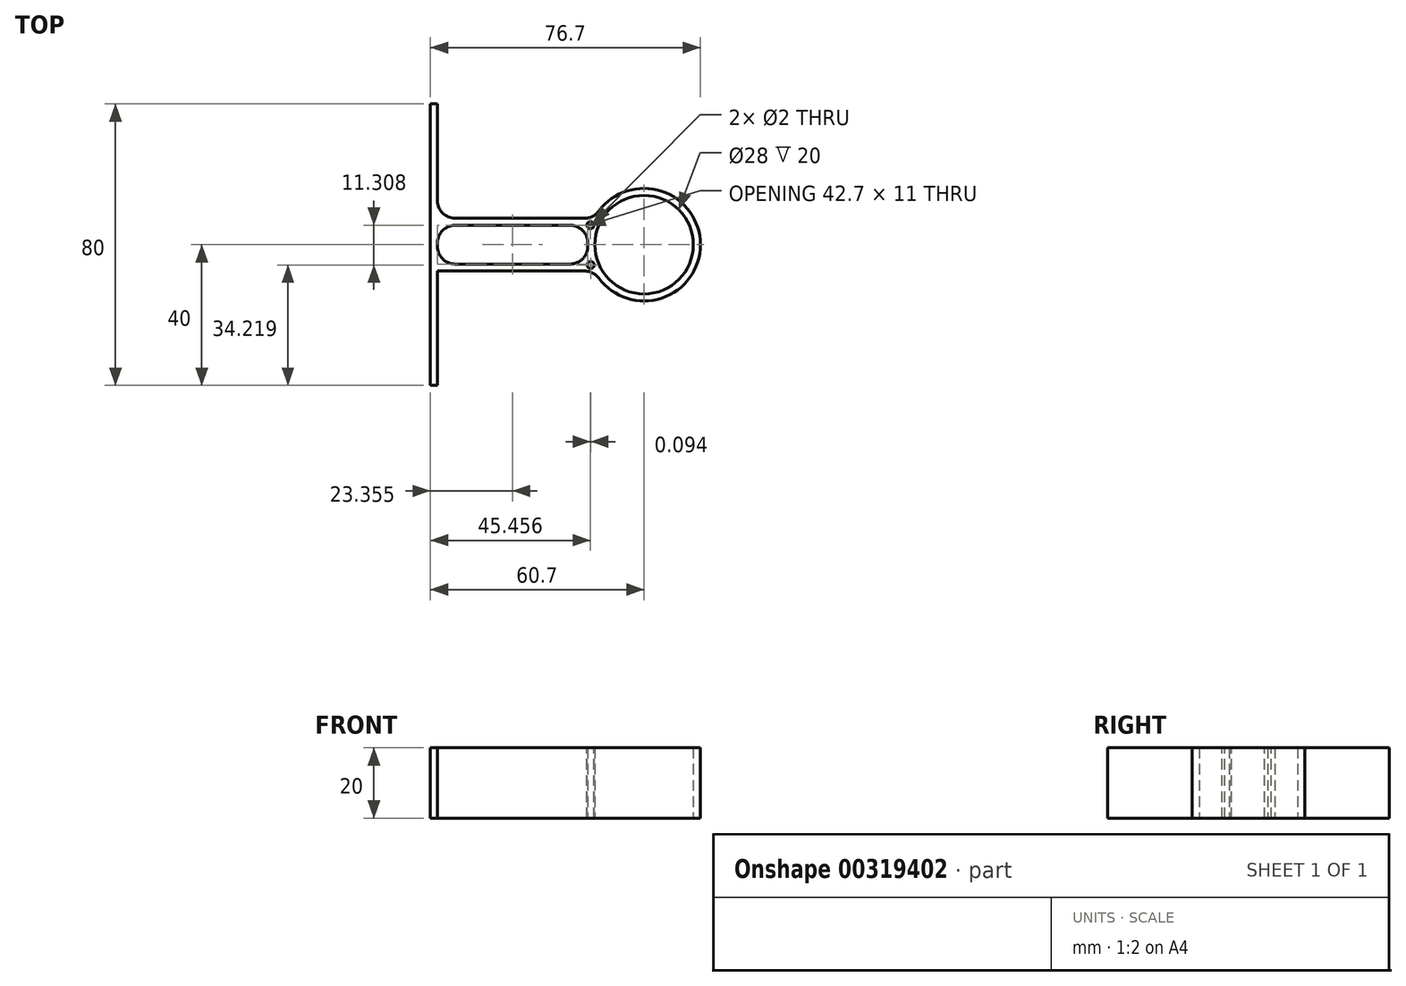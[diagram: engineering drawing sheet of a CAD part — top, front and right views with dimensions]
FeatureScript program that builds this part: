
annotation { "Feature Type Name" : "Feature", "Feature Type Description" : "" }
export const myFeature = defineFeature(function(context is Context, id is Id, definition is map)
    precondition{}
    {
        {
            var Q0;
            Q0=qCreatedBy(makeId("Top.planeOp"),FACE);
            var sketch = newSketch(context, id + "F0", { "sketchPlane" : qUnion([Q0])});
            skCircle(sketch, "E0", {"center": v(0, 0) * mm, "radius": 14 * mm});
            skCircle(sketch, "E1", {"center": v(0, 0) * mm, "radius": 16 * mm});
            skLineSegment(sketch, "E2", {"start": v(-14.13, 7.5) * mm, "end": v(-58.7, 7.5) * mm});
            skLineSegment(sketch, "E3.0", {"start": v(-15.02, 5.5) * mm, "end": v(-58.7, 5.5) * mm});
            skLineSegment(sketch, "E4.0", {"start": v(-58.7, -5.5) * mm, "end": v(-15.02, -5.5) * mm});
            skLineSegment(sketch, "E5.0", {"start": v(-58.7, 5.5) * mm, "end": v(-58.7, -5.5) * mm});
            skLineSegment(sketch, "E6.bottom", {"start": v(-58.7, -40) * mm, "end": v(-60.7, -40) * mm});
            skLineSegment(sketch, "E6.top", {"start": v(-58.7, 40) * mm, "end": v(-60.7, 40) * mm});
            skLineSegment(sketch, "E6.left", {"start": v(-58.7, -40) * mm, "end": v(-58.7, -7.5) * mm});
            skLineSegment(sketch, "E6.right", {"start": v(-60.7, -40) * mm, "end": v(-60.7, 40) * mm});
            skLineSegment(sketch, "E7.trimOffspring", {"start": v(-58.7, -7.5) * mm, "end": v(-14.13, -7.5) * mm});
            skLineSegment(sketch, "E8.trimOffspring", {"start": v(-58.7, 7.5) * mm, "end": v(-58.7, 40) * mm});
            skLineSegment(sketch, "E9.trimOffspring", {"start": v(-58.7, -5.5) * mm, "end": v(-58.7, 5.5) * mm});
            skSolve(sketch);
        }
        {
            var Q0;
            Q0=makeQuery(id+"F0.imprint","IMPRINT",FACE,{"disambiguationData":[TD([[makeQuery(id+"F0.imprint","IMPRINT",EDGE,{"derivedFrom":sQuery(id+"F0.wireOp",EDGE,"E0")}),-1.0]])]});
            var Q1;
            {var subQ0=sQuery(id+"F0.wireOp",EDGE,"E2");Q1=makeQuery(id+"F0.imprint","IMPRINT",FACE,{"disambiguationData":[TD([[makeQuery(id+"F0.imprint","IMPRINT",EDGE,{"derivedFrom":subQ0}),1.0]])]});}
            extrude(context, id + "F1", {"entities" : qUnion([Q0, Q1]), "depth" : 10 * mm, "hasSecondDirection" : true, "secondDirectionOppositeDirection" : true, "secondDirectionDepth" : 10 * mm});
        }
        {
            var Q0;
            Q0=makeQuery(id+"F1.opExtrude","SWEPT_EDGE",EDGE,{"disambiguationData":[OSD([sQuery(id+"F0.wireOp",EDGE,"E1"),sQuery(id+"F0.wireOp",EDGE,"c75a274e-f250-498e-bc5d-d14da76e1f0b.trimOffspring")])]});
            var Q1;
            Q1=makeQuery(id+"F1.opExtrude","SWEPT_EDGE",EDGE,{"disambiguationData":[OSD([sQuery(id+"F0.wireOp",EDGE,"E1"),sQuery(id+"F0.wireOp",EDGE,"E4.0")])]});
            var Q2;
            Q2=makeQuery(id+"F1.opExtrude","SWEPT_EDGE",EDGE,{"disambiguationData":[OSD([sQuery(id+"F0.wireOp",EDGE,"E1"),sQuery(id+"F0.wireOp",EDGE,"E3.0")])]});
            var Q3;
            Q3=makeQuery(id+"F1.opExtrude","SWEPT_EDGE",EDGE,{"disambiguationData":[OSD([sQuery(id+"F0.wireOp",EDGE,"E1"),sQuery(id+"F0.wireOp",EDGE,"E2")])]});
            fillet(context, id + "F2", {"entities" : qUnion([Q0, Q1, Q2, Q3]), "radius" : 5 * mm, "tangentPropagation" : true, "allowEdgeOverflow" : false});
        }
        {
            var Q0;
            Q0=makeQuery(id+"F1.opExtrude","SWEPT_EDGE",EDGE,{"disambiguationData":[OSD([sQuery(id+"F0.wireOp",EDGE,"E4.0"),sQuery(id+"F0.wireOp",EDGE,"E5.0")])]});
            var Q1;
            Q1=makeQuery(id+"F1.opExtrude","SWEPT_EDGE",EDGE,{"disambiguationData":[OSD([sQuery(id+"F0.wireOp",EDGE,"E3.0"),sQuery(id+"F0.wireOp",EDGE,"E5.0")])]});
            fillet(context, id + "F3", {"entities" : qUnion([Q0, Q1]), "radius" : 5 * mm, "tangentPropagation" : true, "allowEdgeOverflow" : false});
        }
        {
            var Q0;
            Q0=makeQuery(id+"F1.opExtrude","CAP_FACE",FACE,{"disambiguationData":[OSD([sQuery(id+"F0.wireOp",EDGE,"E0"),sQuery(id+"F0.wireOp",EDGE,"E1"),sQuery(id+"F0.wireOp",EDGE,"E2"),sQuery(id+"F0.wireOp",EDGE,"sdKVXWY6-Z9S5-hVUQ-U1TP-nAIpewql3z6Z"),sQuery(id+"F0.wireOp",EDGE,"bTCiTOwF-ojJc-qaBJ-uRxB-7UgxpijujMLu"),sQuery(id+"F0.wireOp",EDGE,"E3.0"),sQuery(id+"F0.wireOp",EDGE,"E4.0"),sQuery(id+"F0.wireOp",EDGE,"E5.0")])],"isStart":false});
            var sketch = newSketch(context, id + "F4", { "sketchPlane" : qUnion([Q0])});
            skCircle(sketch, "E10", {"center": v(-15.15, -5.78) * mm, "radius": 1 * mm});
            skLineSegment(sketch, "E11", {"start": v(0, 0) * mm, "end": v(0, 0) * mm});
            skCircle(sketch, "E12.MirrorC", {"center": v(-15.24, 5.53) * mm, "radius": 1 * mm});
            skSolve(sketch);
        }
        {
            var Q0;
            Q0 = qSketchRegion(id + "F4", true);
            extrude(context, id + "F5", {"entities" : qUnion([Q0]), "operationType" : NewBodyOperationType.REMOVE, "oppositeDirection" : true, "depth" : 25 * mm});
        }
        {
            var Q0;
            Q0=makeQuery(id+"F1.opExtrude","SWEPT_EDGE",EDGE,{"disambiguationData":[OSD([sQuery(id+"F0.wireOp",EDGE,"qHgLQr9h-kTCm-Wuth-Ri2y-6xUeRzx2OaRi.right"),sQuery(id+"F0.wireOp",EDGE,"c75a274e-f250-498e-bc5d-d14da76e1f0b.trimOffspring")])]});
            var Q1;
            Q1=makeQuery(id+"F1.opExtrude","SWEPT_EDGE",EDGE,{"disambiguationData":[OSD([sQuery(id+"F0.wireOp",EDGE,"E2"),sQuery(id+"F0.wireOp",EDGE,"744mOC4n-eHFB-99X0-2lT0-6l1oSQom4Ab0.right")])]});
            fillet(context, id + "F6", {"entities" : qUnion([Q0, Q1]), "radius" : 5 * mm, "tangentPropagation" : true, "allowEdgeOverflow" : false});
        }
    });
